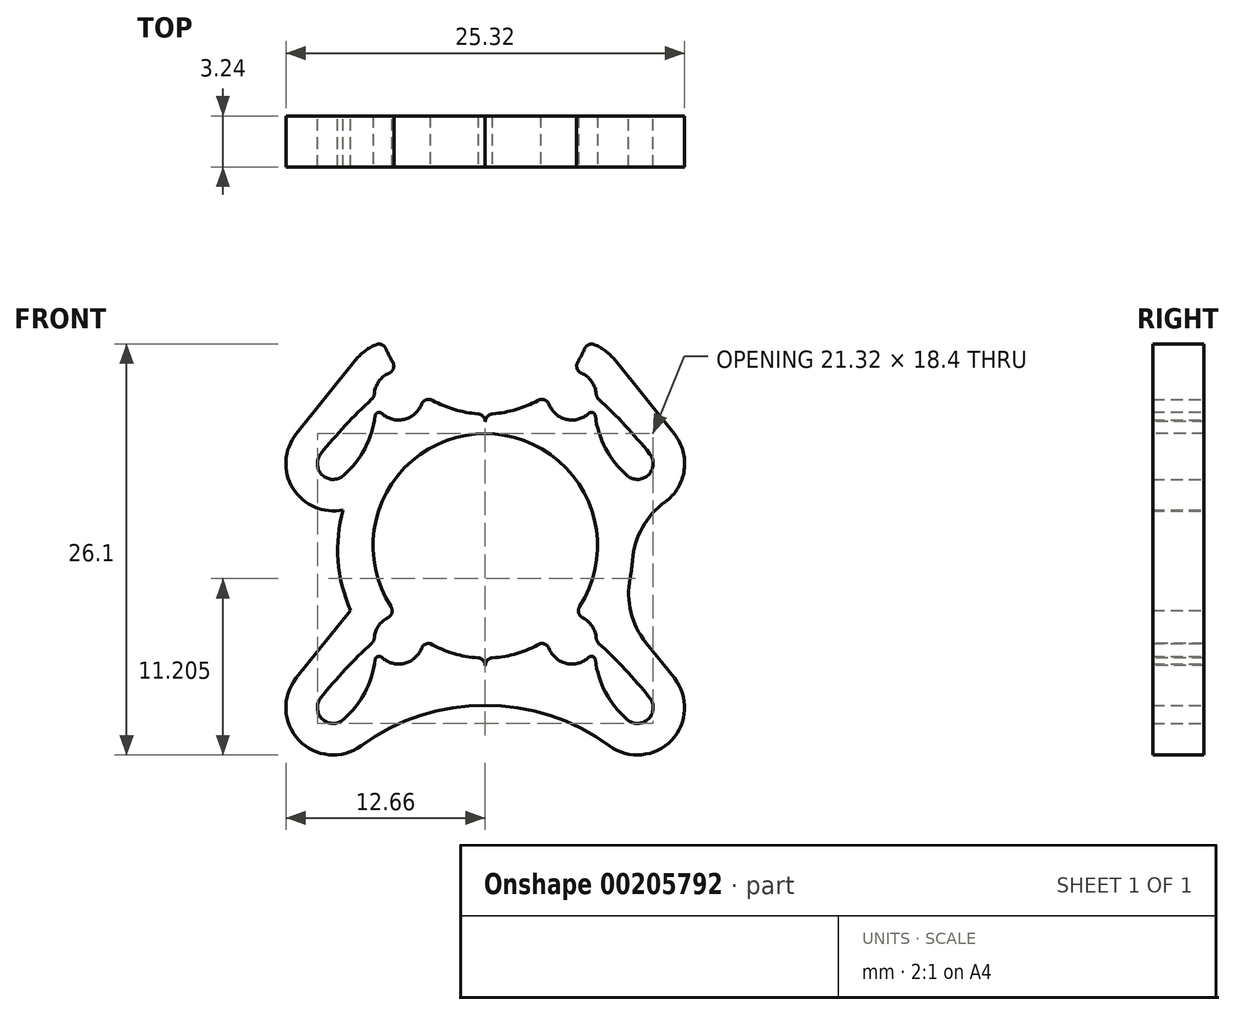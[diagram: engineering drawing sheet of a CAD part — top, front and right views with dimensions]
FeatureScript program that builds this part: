
annotation { "Feature Type Name" : "Feature", "Feature Type Description" : "" }
export const myFeature = defineFeature(function(context is Context, id is Id, definition is map)
    precondition{}
    {
        {
            var Q0;
            Q0=qCreatedBy(makeId("Front.planeOp"),FACE);
            var sketch = newSketch(context, id + "F0", { "sketchPlane" : qUnion([Q0])});
            skCircle(sketch, "E0", {"center": v(0, 0) * mm, "radius": 6.38 * mm});
            skPoint(sketch, "E1", {"position": v(0, 6.38) * mm});
            skPoint(sketch, "E2", {"position": v(0, 11.38) * mm});
            skCircle(sketch, "E3", {"center": v(-5.5, -5.7) * mm, "radius": 1.55 * mm});
            skLineSegment(sketch, "E4", {"start": v(0, 11.38) * mm, "end": v(0, 0) * mm, "construction": true});
            skCircle(sketch, "E5.MirrorC", {"center": v(5.5, -5.7) * mm, "radius": 1.55 * mm});
            skLineSegment(sketch, "E6", {"start": v(-5.5, -5.7) * mm, "end": v(5.5, -5.7) * mm, "construction": true});
            skSolve(sketch);
        }
        {
            var Q0;
            Q0=qCreatedBy(makeId("Front.planeOp"),FACE);
            var sketch = newSketch(context, id + "F1", { "sketchPlane" : qUnion([Q0])});
            skArc(sketch, "E7.0", {"start": v(-3.95, -5.63) * mm, "mid": v(-2.07, -6.56) * mm, "end": v(0, -6.88) * mm});
            skArc(sketch, "E8.3", {"start": v(-6.94, -6.27) * mm, "mid": v(-5.17, -7.22) * mm, "end": v(-3.95, -5.63) * mm});
            skLineSegment(sketch, "E9", {"start": v(0, 0) * mm, "end": v(-9.66, -10.03) * mm, "construction": true});
            skArc(sketch, "E10", {"start": v(-10.44, -9.4) * mm, "mid": v(-10.36, -10.75) * mm, "end": v(-9, -10.78) * mm});
            skLineSegment(sketch, "E11", {"start": v(-5.48, -4.16) * mm, "end": v(-7.05, -5.79) * mm, "construction": true});
            skLineSegment(sketch, "E12", {"start": v(-3.95, -5.63) * mm, "end": v(-5.52, -7.26) * mm, "construction": true});
            skLineSegment(sketch, "E13", {"start": v(-9, -10.78) * mm, "end": v(-4.74, -7.06) * mm, "construction": true});
            skPoint(sketch, "E13.endSnap0", {"position": v(-4.74, -6.44) * mm});
            skLineSegment(sketch, "E14", {"start": v(-6.7, -4.74) * mm, "end": v(-10.44, -9.4) * mm, "construction": true});
            skArc(sketch, "E15.trimOffspring", {"start": v(-6.58, -6.82) * mm, "mid": v(-4.86, -7.12) * mm, "end": v(-3.95, -5.63) * mm});
            skArc(sketch, "E16.trimOffspring", {"start": v(-12, -8.15) * mm, "mid": v(-11.83, -12.1) * mm, "end": v(-7.9, -12.45) * mm});
            skLineSegment(sketch, "E17", {"start": v(0, 0) * mm, "end": v(0, -9.88) * mm, "construction": true});
            skArc(sketch, "E18", {"start": v(0, -9.88) * mm, "mid": v(-4.15, -10.53) * mm, "end": v(-7.9, -12.45) * mm});
            skLineSegment(sketch, "E19", {"start": v(0, -9.88) * mm, "end": v(-5.5, -9.88) * mm, "construction": true});
            skLineSegment(sketch, "E20", {"start": v(0, -9.88) * mm, "end": v(0, -6.88) * mm});
            skArc(sketch, "E21", {"start": v(-5.48, -4.16) * mm, "mid": v(-6.62, -4.63) * mm, "end": v(-7.05, -5.79) * mm});
            skArc(sketch, "E22", {"start": v(-7.05, -5.79) * mm, "mid": v(-8.82, -7.53) * mm, "end": v(-10.44, -9.4) * mm});
            skLineSegment(sketch, "E23", {"start": v(-12, -8.15) * mm, "end": v(-8.27, -3.49) * mm});
            skArc(sketch, "E24", {"start": v(-9, -10.78) * mm, "mid": v(-7.49, -8.75) * mm, "end": v(-6.94, -6.27) * mm});
            skLineSegment(sketch, "E25", {"start": v(-9.66, -13.03) * mm, "end": v(0, -13.03) * mm, "construction": true});
            skLineSegment(sketch, "E26", {"start": v(0, -13.03) * mm, "end": v(0, -6.88) * mm, "construction": true});
            skArc(sketch, "E27", {"start": v(-6.48, -2.3) * mm, "mid": v(-6.05, -3.26) * mm, "end": v(-5.48, -4.16) * mm});
            skArc(sketch, "E28.trimOffspring", {"start": v(-6.48, -2.3) * mm, "mid": v(-7.47, -2.75) * mm, "end": v(-8.27, -3.49) * mm});
            skSolve(sketch);
        }
        {
            var Q0;
            Q0=qSketchRegion(id+"F1",true);
            extrude(context, id + "F2", {"entities" : qUnion([Q0]), "depth" : 3.25 * mm, "symmetric" : true});
        }
        {
            var Q0;
            Q0=makeQuery(id+"F2.opExtrude","SWEPT_EDGE",EDGE,{"disambiguationData":[OSD([sQuery(id+"F1.wireOp",EDGE,"E15.trimOffspring"),sQuery(id+"F1.wireOp",EDGE,"f16a48b5-7a2a-4cbf-833e-9f4b7a7ec827.trimOffspring")])]});
            var Q1;
            Q1=makeQuery(id+"F2.opExtrude","SWEPT_EDGE",EDGE,{"disambiguationData":[OSD([sQuery(id+"F1.wireOp",EDGE,"0503ed2f-4905-41a0-8b90-6c5d83e06de4"),sQuery(id+"F1.wireOp",EDGE,"E15.trimOffspring")])]});
            var Q2;
            Q2=makeQuery(id+"F2.opExtrude","SWEPT_EDGE",EDGE,{"disambiguationData":[OSD([sQuery(id+"F1.wireOp",EDGE,"E7.0"),sQuery(id+"F1.wireOp",EDGE,"E15.trimOffspring")])]});
            var Q3;
            Q3=makeQuery(id+"F2.opExtrude","SWEPT_EDGE",EDGE,{"disambiguationData":[OSD([sQuery(id+"F1.wireOp",EDGE,"E21"),sQuery(id+"F1.wireOp",EDGE,"E22")])]});
            var Q4;
            Q4=makeQuery(id+"F2.opExtrude","SWEPT_EDGE",EDGE,{"disambiguationData":[OSD([sQuery(id+"F1.wireOp",EDGE,"E21"),sQuery(id+"F1.wireOp",EDGE,"aa0188ab-c223-4f96-b803-20454a8c8853")])]});
            var Q5;
            Q5=makeQuery(id+"F2.opExtrude","SWEPT_EDGE",EDGE,{"disambiguationData":[OSD([sQuery(id+"F1.wireOp",EDGE,"e83e305f-1027-4866-97f5-19716599f6f7"),sQuery(id+"F1.wireOp",EDGE,"E15.trimOffspring")])]});
            var Q6;
            Q6=makeQuery(id+"F2.opExtrude","SWEPT_EDGE",EDGE,{"disambiguationData":[OSD([sQuery(id+"F1.wireOp",EDGE,"E10"),sQuery(id+"F1.wireOp",EDGE,"e83e305f-1027-4866-97f5-19716599f6f7")])]});
            var Q7;
            Q7=makeQuery(id+"F2.opExtrude","SWEPT_EDGE",EDGE,{"disambiguationData":[OSD([sQuery(id+"F1.wireOp",EDGE,"MhLNWvLZ-SjSW-ynIw-f0j8-qXF7kueQWDTh"),sQuery(id+"F1.wireOp",EDGE,"wWfipXca-841M-r8ga-aVaF-FZ8B4jg7mFlH")])]});
            fillet(context, id + "F3", {"entities" : qUnion([Q0, Q1, Q2, Q3, Q4, Q5, Q6, Q7]), "radius" : 0.5 * mm, "tangentPropagation" : true, "allowEdgeOverflow" : false});
        }
        {
            var Q0;
            Q0=makeQuery(id+"F2.opExtrude","SWEPT_EDGE",EDGE,{"disambiguationData":[OSD([sQuery(id+"F1.wireOp",EDGE,"E8.3"),sQuery(id+"F1.wireOp",EDGE,"E24")])]});
            fillet(context, id + "F4", {"entities" : qUnion([Q0]), "radius" : .25 * mm, "tangentPropagation" : true, "allowEdgeOverflow" : false});
        }
        {
            var Q0;
            Q0=makeQuery(id+"F2.opExtrude","SWEPT_BODY",BODY,{"disambiguationData":[OSD([sQuery(id+"F1.wireOp",EDGE,"91029bab-c422-4aac-b43c-f8eb8f7441cb.0"),sQuery(id+"F1.wireOp",EDGE,"E7.0"),sQuery(id+"F1.wireOp",EDGE,"E8.0"),sQuery(id+"F1.wireOp",EDGE,"E8.3"),sQuery(id+"F1.wireOp",EDGE,"4fe737ca-cd33-4ae7-bfb5-aca6cdd2fbdd"),sQuery(id+"F1.wireOp",EDGE,"E10"),sQuery(id+"F1.wireOp",EDGE,"87521696-a49b-46d6-ae6d-b95a5258b794"),sQuery(id+"F1.wireOp",EDGE,"3ad451f8-88f0-40d6-b978-8860d0f46c41"),sQuery(id+"F1.wireOp",EDGE,"RmzYGLSE-aIne-cmcq-fouj-xsO9WjanKBXf"),sQuery(id+"F1.wireOp",EDGE,"E1ndacnS-k5oY-T1jz-uEtG-vA6wWoizQWTL"),sQuery(id+"F1.wireOp",EDGE,"290a5299-caae-4b93-a680-34ceb27d99b0"),sQuery(id+"F1.wireOp",EDGE,"acf9eb55-ab42-4665-aab6-df971979b8c6"),sQuery(id+"F1.wireOp",EDGE,"0503ed2f-4905-41a0-8b90-6c5d83e06de4"),sQuery(id+"F1.wireOp",EDGE,"e83e305f-1027-4866-97f5-19716599f6f7"),sQuery(id+"F1.wireOp",EDGE,"E15.trimOffspring"),sQuery(id+"F1.wireOp",EDGE,"E16.trimOffspring"),sQuery(id+"F1.wireOp",EDGE,"140a15c2-b3ae-4d8c-875c-2f7ce67bd9a0.trimOffspring"),sQuery(id+"F1.wireOp",EDGE,"f16a48b5-7a2a-4cbf-833e-9f4b7a7ec827.trimOffspring"),sQuery(id+"F1.wireOp",EDGE,"c726c67e-1b0a-4414-994c-10f8da0a7d9b.trimOffspring"),sQuery(id+"F1.wireOp",EDGE,"E18"),sQuery(id+"F1.wireOp",EDGE,"9d4cf9fb-cccf-4056-9c7a-a0118e21bfc9.trimOffspring"),sQuery(id+"F1.wireOp",EDGE,"aw0qZEzT-GYTq-v6Y8-Owwz-bXgHvjQE39bA"),sQuery(id+"F1.wireOp",EDGE,"E20"),sQuery(id+"F1.wireOp",EDGE,"e7ad43b5-d072-4a5a-872d-9ebe676b2ed9.trimOffspring")])]});
            var Q1;
            Q1=qCreatedBy(makeId("Right.planeOp"),FACE);
            mirror(context, id + "F5", {"operationType" : NewBodyOperationType.ADD, "entities" : qUnion([Q0]), "mirrorPlane" : qUnion([Q1])});
        }
        {
            var Q0;
            Q0=makeQuery(id+"F2.opExtrude","SWEPT_EDGE",EDGE,{"disambiguationData":[OSD([sQuery(id+"F1.wireOp",EDGE,"E27"),sQuery(id+"F1.wireOp",EDGE,"E28.trimOffspring")])]});
            var Q1;
            Q1=makeQuery(id+"F5.opPattern","COPY",EDGE,{"derivedFrom":makeQuery(id+"F2.opExtrude","SWEPT_EDGE",EDGE,{"disambiguationData":[OSD([sQuery(id+"F1.wireOp",EDGE,"E27"),sQuery(id+"F1.wireOp",EDGE,"E28.trimOffspring")])]}),"instanceName":"1"});
            fillet(context, id + "F6", {"entities" : qUnion([Q0, Q1]), "radius" : .5 * mm, "tangentPropagation" : true, "allowEdgeOverflow" : false});
        }
        {
            var Q0;
            Q0=makeQuery(id+"F2.opExtrude","SWEPT_BODY",BODY,{"disambiguationData":[OSD([sQuery(id+"F1.wireOp",EDGE,"E7.0"),sQuery(id+"F1.wireOp",EDGE,"E10"),sQuery(id+"F1.wireOp",EDGE,"E15.trimOffspring"),sQuery(id+"F1.wireOp",EDGE,"E16.trimOffspring"),sQuery(id+"F1.wireOp",EDGE,"E18"),sQuery(id+"F1.wireOp",EDGE,"E20"),sQuery(id+"F1.wireOp",EDGE,"E21"),sQuery(id+"F1.wireOp",EDGE,"E22"),sQuery(id+"F1.wireOp",EDGE,"E23"),sQuery(id+"F1.wireOp",EDGE,"E24"),sQuery(id+"F1.wireOp",EDGE,"E27"),sQuery(id+"F1.wireOp",EDGE,"E28.trimOffspring")])]});
            transform(context, id + "F7", {"entities" : qUnion([Q0]), "transformType" : TransformType.TRANSLATION_3D, "dx" : 0 * mm, "dy" : 0 * mm, "dz" : 15.5 * mm, "makeCopy" : true});
        }
        {
            var Q0;
            Q0=qCreatedBy(makeId("Front.planeOp"),FACE);
            var sketch = newSketch(context, id + "F8", { "sketchPlane" : qUnion([Q0])});
            skArc(sketch, "E29", {"start": v(5.95, -3.44) * mm, "mid": v(6.77, 1.2) * mm, "end": v(4.42, 5.27) * mm});
            skArc(sketch, "E30", {"start": v(8.12, -4.69) * mm, "mid": v(9.23, 1.63) * mm, "end": v(6.03, 7.18) * mm});
            skLineSegment(sketch, "E31", {"start": v(-8.12, -4.69) * mm, "end": v(-5.95, -3.44) * mm});
            skLineSegment(sketch, "E32", {"start": v(0, 0) * mm, "end": v(0, 9.38) * mm, "construction": true});
            skLineSegment(sketch, "E33.MirrorCS", {"start": v(8.12, -4.69) * mm, "end": v(5.95, -3.44) * mm});
            skLineSegment(sketch, "E34", {"start": v(-5.95, -3.44) * mm, "end": v(0, 0) * mm, "construction": true});
            skLineSegment(sketch, "E35", {"start": v(0, 0) * mm, "end": v(-4.42, 5.27) * mm, "construction": true});
            skLineSegment(sketch, "E36", {"start": v(-4.42, 5.27) * mm, "end": v(-6.03, 7.18) * mm});
            skLineSegment(sketch, "E37.MirrorCS", {"start": v(4.42, 5.27) * mm, "end": v(6.03, 7.18) * mm});
            skLineSegment(sketch, "E38.MirrorCS", {"start": v(0, 0) * mm, "end": v(4.42, 5.27) * mm, "construction": true});
            skArc(sketch, "E39.trimOffspring", {"start": v(-6.03, 7.18) * mm, "mid": v(-9.23, 1.63) * mm, "end": v(-8.12, -4.69) * mm});
            skArc(sketch, "E40.trimOffspring", {"start": v(-4.42, 5.27) * mm, "mid": v(-6.77, 1.2) * mm, "end": v(-5.95, -3.44) * mm});
            skSolve(sketch);
        }
        {
            var Q0;
            Q0 = qSketchRegion(id + "F8", true);
            extrude(context, id + "F9", {"entities" : qUnion([Q0]), "operationType" : NewBodyOperationType.ADD, "depth" : 3.25 * mm, "symmetric" : true});
        }
        {
            var Q0;
            {var subQ0=sQuery(id+"F1.wireOp",EDGE,"E28.trimOffspring");var subQ1=sQuery(id+"F1.wireOp",EDGE,"E27");Q0=makeQuery(id+"F9.boolean.opBoolean","INTERSECT",EDGE,{"derivedFrom":[makeQuery(id+"F6.opFillet","BLEND_FACE",FACE,{"disambiguationData":[OSD([subQ1,subQ0]),TDD([makeQuery(id+"F2.opExtrude","SWEPT_EDGE",EDGE,{"disambiguationData":[OSD([subQ1,subQ0])]})])]}),makeQuery(id+"F9.opExtrude","SWEPT_FACE",FACE,{"disambiguationData":[OSD([sQuery(id+"F8.wireOp",EDGE,"E29")])]})]});}
            var Q1;
            {var subQ0=sQuery(id+"F1.wireOp",EDGE,"E28.trimOffspring");var subQ1=sQuery(id+"F1.wireOp",EDGE,"E27");Q1=makeQuery(id+"F9.boolean.opBoolean","INTERSECT",EDGE,{"derivedFrom":[makeQuery(id+"F6.opFillet","BLEND_FACE",FACE,{"disambiguationData":[OSD([subQ1,subQ0]),TDD([makeQuery(id+"F5.opPattern","COPY",EDGE,{"derivedFrom":makeQuery(id+"F2.opExtrude","SWEPT_EDGE",EDGE,{"disambiguationData":[OSD([subQ1,subQ0])]}),"instanceName":"1"})])]}),makeQuery(id+"F9.opExtrude","SWEPT_FACE",FACE,{"disambiguationData":[OSD([sQuery(id+"F8.wireOp",EDGE,"E29")])]})]});}
            var Q2;
            Q2=makeQuery(id+"F9.boolean.opBoolean","INTERSECT",EDGE,{"derivedFrom":[makeQuery(id+"F2.opExtrude","SWEPT_FACE",FACE,{"disambiguationData":[OSD([sQuery(id+"F1.wireOp",EDGE,"E23")])]}),makeQuery(id+"F9.opExtrude","SWEPT_FACE",FACE,{"disambiguationData":[OSD([sQuery(id+"F8.wireOp",EDGE,"E30")])]})]});
            var Q3;
            Q3=makeQuery(id+"F9.boolean.opBoolean","INTERSECT",EDGE,{"derivedFrom":[makeQuery(id+"F5.opPattern","COPY",FACE,{"derivedFrom":makeQuery(id+"F2.opExtrude","SWEPT_FACE",FACE,{"disambiguationData":[OSD([sQuery(id+"F1.wireOp",EDGE,"E23")])]}),"instanceName":"1"}),makeQuery(id+"F9.opExtrude","SWEPT_FACE",FACE,{"disambiguationData":[OSD([sQuery(id+"F8.wireOp",EDGE,"E30")])]})]});
            var Q4;
            Q4=makeQuery(id+"F9.boolean.opBoolean","INTERSECT",EDGE,{"derivedFrom":[makeQuery(id+"F7.opPattern","COPY",FACE,{"derivedFrom":makeQuery(id+"F2.opExtrude","SWEPT_FACE",FACE,{"disambiguationData":[OSD([sQuery(id+"F1.wireOp",EDGE,"E16.trimOffspring")])]}),"instanceName":"1"}),makeQuery(id+"F9.opExtrude","SWEPT_FACE",FACE,{"disambiguationData":[OSD([sQuery(id+"F8.wireOp",EDGE,"E30")])]})]});
            var Q5;
            Q5=makeQuery(id+"F9.boolean.opBoolean","INTERSECT",EDGE,{"derivedFrom":[makeQuery(id+"F7.opPattern","COPY",FACE,{"derivedFrom":makeQuery(id+"F5.opPattern","COPY",FACE,{"derivedFrom":makeQuery(id+"F2.opExtrude","SWEPT_FACE",FACE,{"disambiguationData":[OSD([sQuery(id+"F1.wireOp",EDGE,"E16.trimOffspring")])]}),"instanceName":"1"}),"instanceName":"1"}),makeQuery(id+"F9.opExtrude","SWEPT_FACE",FACE,{"disambiguationData":[OSD([sQuery(id+"F8.wireOp",EDGE,"E30")])]})]});
            fillet(context, id + "F10", {"entities" : qUnion([Q0, Q1, Q2, Q3, Q4, Q5]), "radius" : 5 * mm, "tangentPropagation" : true, "allowEdgeOverflow" : false});
        }
        {
            var Q0;
            Q0=qCreatedBy(makeId("Front.planeOp"),FACE);
            var sketch = newSketch(context, id + "F11", { "sketchPlane" : qUnion([Q0])});
            skCircle(sketch, "E41", {"center": v(0, 0.25) * mm, "radius": 7.13 * mm});
            skPoint(sketch, "E42", {"position": v(0, -6.88) * mm});
            skSolve(sketch);
        }
        {
            var Q0;
            Q0 = qSketchRegion(id + "F11", true);
            extrude(context, id + "F12", {"entities" : qUnion([Q0]), "operationType" : NewBodyOperationType.REMOVE, "endBound" : BoundingType.THROUGH_ALL, "oppositeDirection" : true, "depth" : 25 * mm, "hasSecondDirection" : true, "secondDirectionBound" : BoundingType.THROUGH_ALL, "secondDirectionOppositeDirection" : false, "secondDirectionDepth" : 25 * mm});
        }
        {
            var Q0;
            Q0=makeQuery(id+"F12.boolean.opBoolean","INTERSECT",EDGE,{"derivedFrom":[makeQuery(id+"F3.opFillet","BLEND_FACE",FACE,{"disambiguationData":[OSD([sQuery(id+"F1.wireOp",EDGE,"E21"),sQuery(id+"F1.wireOp",EDGE,"E27")])]}),makeQuery(id+"F12.opExtrude","SWEPT_FACE",FACE,{"disambiguationData":[OSD([sQuery(id+"F11.wireOp",EDGE,"E41")])]})]});
            var Q1;
            Q1=makeQuery(id+"F12.boolean.opBoolean","INTERSECT",EDGE,{"derivedFrom":[makeQuery(id+"F5.opPattern","COPY",FACE,{"derivedFrom":makeQuery(id+"F3.opFillet","BLEND_FACE",FACE,{"disambiguationData":[OSD([sQuery(id+"F1.wireOp",EDGE,"E21"),sQuery(id+"F1.wireOp",EDGE,"E27")])]}),"instanceName":"1"}),makeQuery(id+"F12.opExtrude","SWEPT_FACE",FACE,{"disambiguationData":[OSD([sQuery(id+"F11.wireOp",EDGE,"E41")])]})]});
            fillet(context, id + "F13", {"entities" : qUnion([Q0, Q1]), "radius" : .5 * mm, "tangentPropagation" : true, "allowEdgeOverflow" : false});
        }
    });
